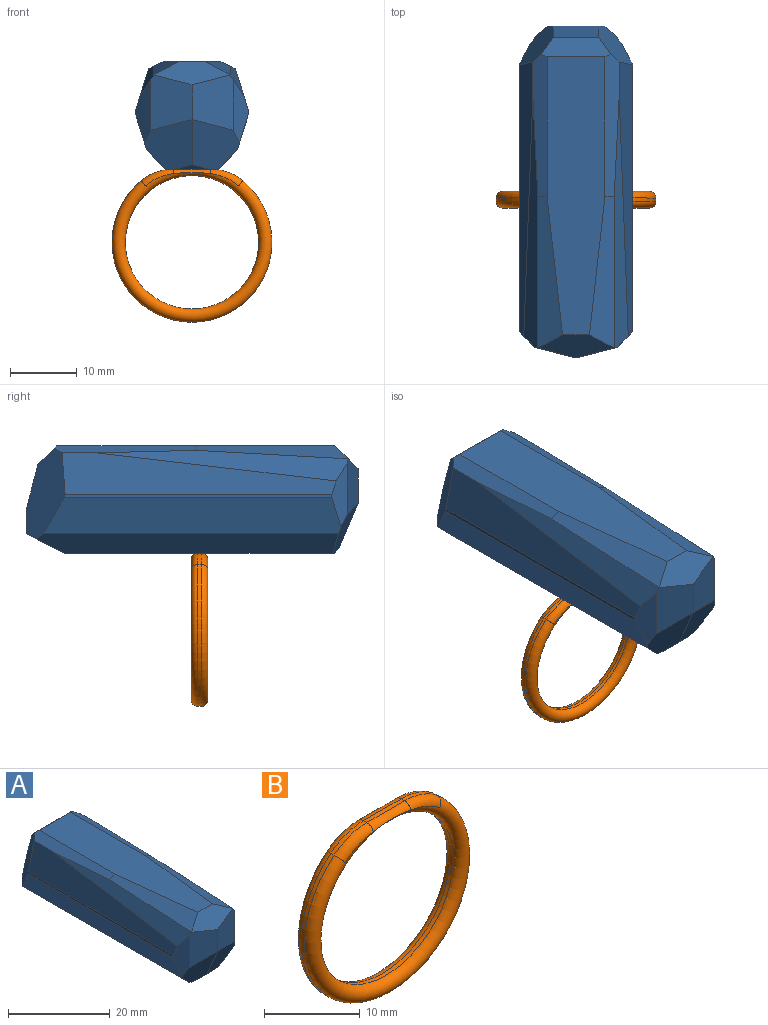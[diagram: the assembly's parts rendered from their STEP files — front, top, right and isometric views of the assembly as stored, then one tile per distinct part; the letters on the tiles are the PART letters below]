
ASSEMBLY  parts=2 mates=1
PART A: 33 faces, bbox 17x49.8x16.1 mm
  f0: plane 45.32x2.9mm, normal (0.71,0,-0.71), area 177.5mm2, adj f6,f8,f14,f16,f18
  f1: plane 9.49x2.3mm, normal (0.71,-0.71,0), area 19.1mm2, adj f5,f9,f13,f14,f17,f18
  f2: plane 22.75x3.71mm, normal (0.45,-0.05,0.89), area 63.4mm2, adj f4,f5,f10,f15,f17
  f3: plane 4.82x0.63mm, normal (0,-0.71,-0.71), area 2.1mm2, adj f8,f18,f19
  f4: plane 11.46x3.46mm, normal (0,-0.71,0.71), area 33.7mm2, adj f2,f15,f17,f20,f27
  f5: plane 37.76x4.6mm, normal (0.85,-0.03,0.53), area 91.5mm2, adj f1,f2,f10,f13,f17
  f6: plane 13.6x5.87mm, normal (0.71,0.68,0.18), area 72.8mm2, adj f0,f7,f9,f10,f11,f12,f13,f14
  f7: plane 8.62x3.52mm, normal (0,1,0), area 27.2mm2, adj f6,f12,f16,f25
  f8: plane 40.54x7.84mm, normal (0,0,-1), area 317.6mm2, adj f0,f3,f16,f18,f19,f29
  f9: plane 40.18x0.52mm, normal (1,0,0), area 20.7mm2, adj f1,f6,f13,f14
  f10: plane 21.38x2.14mm, normal (0.45,0,0.89), area 43.8mm2, adj f2,f5,f6,f11,f13,f15
  f11: plane 10.3x2.82mm, normal (0,0.71,0.71), area 34.7mm2, adj f6,f10,f12,f15,f23,f25
  f12: plane 6.88x6.84mm, normal (0,0.97,0.25), area 48.6mm2, adj f6,f7,f11,f25
  f13: plane 41.15x6.24mm, normal (0.95,0,0.31), area 188mm2, adj f1,f5,f6,f9,f10
  f14: plane 44.68x5.39mm, normal (0.95,0,-0.3), area 240mm2, adj f0,f1,f6,f9,f18
  f15: plane 41.76x8.69mm, normal (0,0,1), area 314.6mm2, adj f2,f4,f10,f11,f23,f27
  f16: plane 12.07x5.8mm, normal (0,0.45,-0.89), area 65.3mm2, adj f0,f6,f7,f8,f25,f29
  f17: plane 8.34x6.2mm, normal (0.25,-0.97,0), area 43.6mm2, adj f1,f2,f4,f5,f18,f20
  f18: plane 7.43x7.14mm, normal (0.14,-0.91,-0.39), area 43.4mm2, adj f0,f1,f3,f8,f14,f17,f19
  f19: plane 7.43x7.14mm, normal (-0.14,-0.91,-0.39), area 43.4mm2, adj f3,f8,f18,f20,f21,f28,f29
  f20: plane 8.34x6.2mm, normal (-0.25,-0.97,0), area 43.6mm2, adj f4,f17,f19,f26,f27,f28
  f21: plane 44.68x5.39mm, normal (-0.95,0,-0.3), area 240mm2, adj f19,f24,f25,f28,f29
  f22: plane 41.15x6.24mm, normal (-0.95,0,0.31), area 188mm2, adj f23,f24,f25,f26,f28
  f23: plane 21.38x2.14mm, normal (-0.45,0,0.89), area 43.8mm2, adj f11,f15,f22,f25,f26,f27
  f24: plane 40.18x0.52mm, normal (-1,0,0), area 20.7mm2, adj f21,f22,f25,f28
  f25: plane 13.6x5.87mm, normal (-0.71,0.68,0.18), area 72.8mm2, adj f7,f11,f12,f16,f21,f22,f23,f24
  f26: plane 37.76x4.6mm, normal (-0.85,-0.03,0.53), area 91.5mm2, adj f20,f22,f23,f27,f28
  f27: plane 22.75x3.71mm, normal (-0.45,-0.05,0.89), area 63.4mm2, adj f4,f15,f20,f23,f26
  f28: plane 9.49x2.3mm, normal (-0.71,-0.71,0), area 19.1mm2, adj f19,f20,f21,f22,f24,f26
  f29: plane 45.32x2.9mm, normal (-0.71,0,-0.71), area 177.5mm2, adj f8,f16,f19,f21,f25
  f30: plane 15x15mm, normal (0,1,0), area 176.7mm2, adj f32
  f31: plane 15x15mm, normal (0,-1,0), area 176.7mm2, adj f32
  f32: cylinder r=7.5mm len=40mm, axis (0,1,0), area 1885mm2, adj f30,f31
PART B: 13 faces, bbox 26x2.5x26 mm
  f0: plane 5.57x0.5mm, normal (0,0,1), area 2.8mm2, adj f3,f4,f8,f12
  f1: cylinder r=10mm len=20mm, axis (0,1,0), area 31.4mm2, adj f5,f9
  f2: cylinder r=12mm len=24mm, axis (0,1,0), area 29.4mm2, adj f3,f4,f5,f9
  f3: cylinder r=7.62mm len=4.85mm, axis (0,1,0), area 2.6mm2, adj f0,f2,f7,f10
  f4: cylinder r=7.62mm len=4.85mm, axis (0,1,0), area 2.6mm2, adj f0,f2,f6,f11
  f5: torus R=11mm, axis (0,-1,0), area 187.9mm2, adj f1,f2,f6,f7,f8
  f6: torus R=6.62mm, axis (0,-1,0), area 7.1mm2, adj f4,f5,f8
  f7: torus R=6.62mm, axis (0,-1,0), area 7.1mm2, adj f3,f5,f8
  f8: cylinder r=1mm len=5.57mm, axis (1,0,0), area 6.2mm2, adj f0,f5,f6,f7
  f9: torus R=11mm, axis (0,-1,0), area 187.9mm2, adj f1,f2,f10,f11,f12
  f10: torus R=6.62mm, axis (0,-1,0), area 7.1mm2, adj f3,f9,f12
  f11: torus R=6.62mm, axis (0,-1,0), area 7.1mm2, adj f4,f9,f12
  f12: cylinder r=1mm len=5.57mm, axis (-1,0,0), area 6.2mm2, adj f0,f9,f10,f11
PLACE A t=(42.82,24.36,18.81)mm
PLACE B t=(42.82,25.56,-0.27)mm
MATE fastened A.f8 <-> B.f0  axis (0,0,-1) through (42.82,24.31,10.73)mm
